# Revit family: 201_DINO-T-_-Back
name_source: partatom
category: Air Terminals
units: mm (PartAtom-declared; Revit-internal decimal feet)

## family parameters
Always vertical = Yes
Cut with Voids When Loaded = No
Part Type = Normal
Room Calculation Point = Yes
Round Connector Dimension = Use Diameter
Shared = No
Work Plane-Based = No

## types (6) — shared parameters
CAT0 = Yes
CL_Location_5000 = 5000 mm  [stored 16.4042 ft]
D2 = 115 mm  [stored 0.377297 ft]
Description = Flush mounted Displacement device. Connection from the back
E1 = 15 mm  [stored 0.0492126 ft]
EL = 340 mm  [stored 1.11549 ft]
EL__ve = -340 mm  [stored -1.11549 ft]
H1 = 600 mm  [stored 1.9685 ft]
H1__ve = -600 mm  [stored -1.9685 ft]
L_ARR = 400 mm  [stored 1.31234 ft]
Manufacturer = Climecon
QmdConnectorList = 201;D
URL = www.climecon.fi
W_ARR = 400 mm  [stored 1.31234 ft]
X1 = No
X2 = No
X3 = No
X4 = No
XRefLineVPlnId = 7453
Y1 = No
Y2 = No
Y3 = No
Y4 = No
Y5 = No
YRefLineVPlnId = 7456
Z1 = No
Z2 = No
Z3 = No
Z4 = No
Z5 = No
magiPartTypeId = 201
magiProductFamilyId = DINO-T-*-Back
zero-valued in all types: CLBTZ, H_ARR, MC_Default_elevation

## per-type parameters (varying)
| type | AA | B1 | C | C__ve | D | E | R |
| DINO-T-125-Back | 295 mm  [stored 0.967848 ft] | 295 mm  [stored 0.967848 ft] | 255 mm  [stored 0.836614 ft] | -255 mm  [stored -0.836614 ft] | 125 mm | 143 mm  [stored 0.46916 ft] | 63 mm |
| DINO-T-400-Back | 595 mm  [stored 1.9521 ft] | 995 mm  [stored 3.26444 ft] | 540 mm  [stored 1.77165 ft] | -540 mm  [stored -1.77165 ft] | 400 mm | 280 mm  [stored 0.918635 ft] | 200 mm  [stored 0.656168 ft] |
| DINO-T-315-Back | 595 mm  [stored 1.9521 ft] | 995 mm  [stored 3.26444 ft] | 440 mm  [stored 1.44357 ft] | -440 mm  [stored -1.44357 ft] | 315 mm | 238 mm  [stored 0.78084 ft] | 158 mm |
| DINO-T-250-Back | 295 mm  [stored 0.967848 ft] | 995 mm  [stored 3.26444 ft] | 395 mm  [stored 1.29593 ft] | -395 mm  [stored -1.29593 ft] | 250 mm | 205 mm  [stored 0.672572 ft] | 125 mm  [stored 0.410105 ft] |
| DINO-T-200-Back | 295 mm  [stored 0.967848 ft] | 595 mm  [stored 1.9521 ft] | 345 mm  [stored 1.13189 ft] | -345 mm  [stored -1.13189 ft] | 200 mm | 180 mm  [stored 0.590551 ft] | 100 mm  [stored 0.328084 ft] |
| DINO-T-160-Back | 295 mm  [stored 0.967848 ft] | 295 mm  [stored 0.967848 ft] | 310 mm  [stored 1.01706 ft] | -310 mm  [stored -1.01706 ft] | 160 mm | 160 mm  [stored 0.524934 ft] | 80 mm  [stored 0.262467 ft] |

note: column(s) folded — value = type name in every type: magiProductCode, magiProductId

note: [stored X ft] marks values corroborated as IEEE doubles in the binary element streams (Revit-internal decimal feet)
